# Revit family: 57_ME_UN_HRC-300-500 links_Orcon
name_source: partatom
category: Mechanical Equipment
units: mm (PartAtom-declared; Revit-internal decimal feet)

## family parameters
Always vertical = Yes
Cut with Voids When Loaded = No
OmniClass Number = 23.75.10.34.21
OmniClass Title = Heat Exchangers for Ventilation Air
Part Type = Normal
Room Calculation Point = No
Round Connector Dimension = Use Diameter
Shared = No
Work Plane-Based = No

## types (6) — shared parameters
Black = Color RGB 076-076-076
Blue = Color RGB 000-137-182
Depth = 602 mm  [stored 1.97507 ft]
Description = Orcon WTW woonhuis HRC
GLN = 8718403860009
Grey = Color RGB 128-128-128
Height = 888 mm  [stored 2.91339 ft]
Hertz = 50 Hz
IFCExportAs = IfcHeatExchanger
IFCExportType = NOTDEFINED
Manufacturer = Orcon
Return Angle = 90.00°
Return Length = 132.3 mm  [stored 0.434055 ft]
Return Side Cap = Yes
Return Top Cap = No
Return Top Connection = Yes
Sanitary Diameter = 32 mm  [stored 0.104987 ft]
Supply1 Angle = 90.00°
Supply1 Length = 132.3 mm  [stored 0.434055 ft]
Supply1 Side Cap = Yes
Supply1 Top Cap = No
Supply1 Top Connection = Yes
Voltage = 230 V
White = Color RAL 9016
Width = 760 mm  [stored 2.49344 ft]
zero-valued in all types: Default Elevation

## per-type parameters (varying)
| type | Airflow Rate (m3/h) | Diameter Inner | Duct Diameter | GTIN | Power | Side Blue | Unit Weight (kg) | artikelnummer |
| HRC-300-EcoMax | 300 | 148 mm  [stored 0.485564 ft] | 150 mm  [stored 0.492126 ft] | 8718403860108 | 73 VA | Color RGB 000-137-182 | 34 | 22000080 |
| HRC-300-MaxComfort | 300 | 148 mm  [stored 0.485564 ft] | 150 mm  [stored 0.492126 ft] | 8718403860115 | 73 VA | Color RGB 000-137-182 | 34 | 22000085 |
| HRC-400-EcoMax | 400 | 178 mm  [stored 0.58399 ft] | 180 mm  [stored 0.590551 ft] | 8718403860122 | 170 VA | Color RGB 000-137-182 | 35 | 22000090 |
| HRC-400-MaxComfort | 400 | 178 mm  [stored 0.58399 ft] | 180 mm  [stored 0.590551 ft] | 8718403860139 | 170 VA | Color RGB 000-137-182 | 35 | 22000095 |
| HRC-500-EcoMax | 500 | 178 mm  [stored 0.58399 ft] | 180 mm  [stored 0.590551 ft] | 8718403863314 | 170 VA | Color RGB 076-076-076 | 34 | 22000100 |
| HRC-500-MaxComfort | 500 | 178 mm  [stored 0.58399 ft] | 180 mm  [stored 0.590551 ft] | 8718403863321 | 170 VA | Color RGB 076-076-076 | 34 | 22000105 |

note: column(s) folded — value = type name in every type: Model

note: [stored X ft] marks values corroborated as IEEE doubles in the binary element streams (Revit-internal decimal feet)

## geometry (parser evidence)
native form markers: Sweep x10
no freeform markers — native parametric forms only
